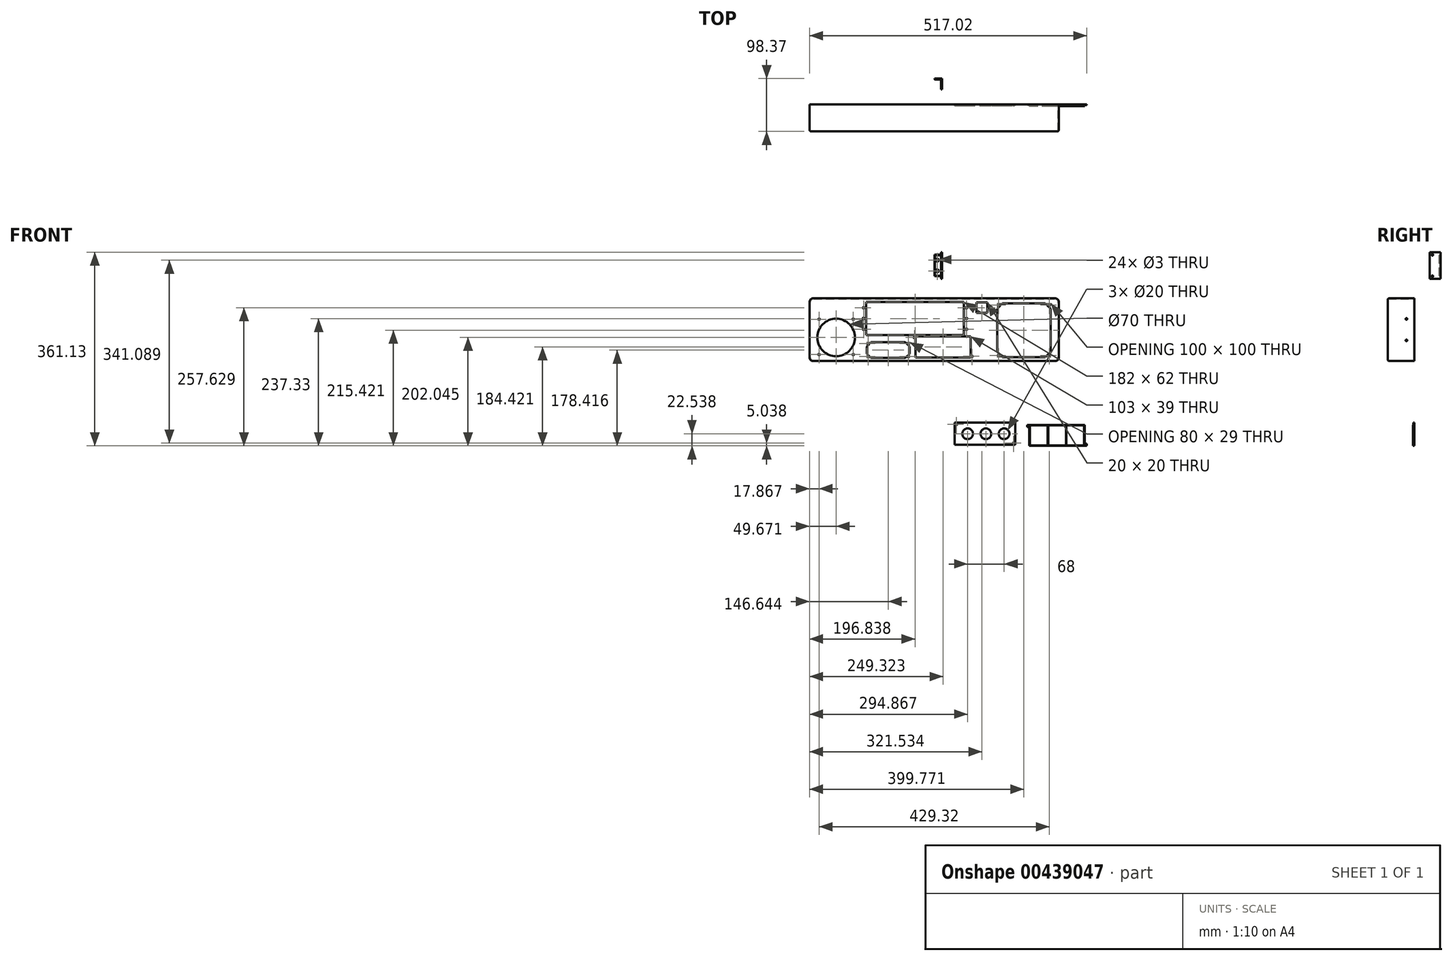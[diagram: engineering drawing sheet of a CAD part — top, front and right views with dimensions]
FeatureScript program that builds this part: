
annotation { "Feature Type Name" : "Feature", "Feature Type Description" : "" }
export const myFeature = defineFeature(function(context is Context, id is Id, definition is map)
    precondition{}
    {
        {
            var Q0;
            Q0=qCreatedBy(makeId("Front.planeOp"),FACE);
            var sketch = newSketch(context, id + "F0", { "sketchPlane" : qUnion([Q0])});
            skLineSegment(sketch, "E0.bottom", {"start": v(-245.15, 85.69) * mm, "end": v(219.85, 85.69) * mm});
            skLineSegment(sketch, "E0.top", {"start": v(-245.15, -31.31) * mm, "end": v(219.85, -31.31) * mm});
            skLineSegment(sketch, "E0.left", {"start": v(-245.15, 85.69) * mm, "end": v(-245.15, -31.31) * mm});
            skLineSegment(sketch, "E0.right", {"start": v(219.85, 85.69) * mm, "end": v(219.85, -31.31) * mm});
            skSolve(sketch);
        }
        {
            var Q0;
            Q0=qSketchRegion(id+"F0",true);
            var Q1;
            Q1=makeQuery(id+"F0.imprint","IMPRINT",FACE,{"disambiguationData":[TD([[makeQuery(id+"F0.imprint","IMPRINT",EDGE,{"derivedFrom":sQuery(id+"F0.wireOp",EDGE,"E0.bottom")}),-1.0]])]});
            extrude(context, id + "F1", {"entities" : qUnion([Q0, Q1]), "depth" : 50 * mm});
        }
        {
            var Q0;
            Q0=makeQuery(id+"F1.opExtrude","CAP_FACE",FACE,{"disambiguationData":[OSD([sQuery(id+"F0.wireOp",EDGE,"E0.bottom"),sQuery(id+"F0.wireOp",EDGE,"E0.top"),sQuery(id+"F0.wireOp",EDGE,"E0.left"),sQuery(id+"F0.wireOp",EDGE,"E0.right")])],"isStart":true});
            shell(context, id + "F2", {"entities" : qUnion([Q0]), "thickness" : 1 * mm});
        }
        {
            var Q0;
            Q0=makeQuery(id+"F1.opExtrude","CAP_FACE",FACE,{"disambiguationData":[OSD([sQuery(id+"F0.wireOp",EDGE,"E0.bottom"),sQuery(id+"F0.wireOp",EDGE,"E0.top"),sQuery(id+"F0.wireOp",EDGE,"E0.left"),sQuery(id+"F0.wireOp",EDGE,"E0.right")])],"isStart":false});
            var sketch = newSketch(context, id + "F3", { "sketchPlane" : qUnion([Q0])});
            skLineSegment(sketch, "E1.bottom", {"start": v(-139.31, 79.02) * mm, "end": v(42.69, 79.02) * mm});
            skLineSegment(sketch, "E1.top", {"start": v(-139.31, 17.02) * mm, "end": v(42.69, 17.02) * mm});
            skLineSegment(sketch, "E1.left", {"start": v(-139.31, 79.02) * mm, "end": v(-139.31, 17.02) * mm});
            skLineSegment(sketch, "E1.right", {"start": v(42.69, 79.02) * mm, "end": v(42.69, 17.02) * mm});
            skLineSegment(sketch, "E2.bottom", {"start": v(66.38, 78.32) * mm, "end": v(86.38, 78.32) * mm});
            skLineSegment(sketch, "E2.top", {"start": v(66.38, 58.32) * mm, "end": v(86.38, 58.32) * mm});
            skLineSegment(sketch, "E2.left", {"start": v(66.38, 78.32) * mm, "end": v(66.38, 58.32) * mm});
            skLineSegment(sketch, "E2.right", {"start": v(86.38, 78.32) * mm, "end": v(86.38, 58.32) * mm});
            skLineSegment(sketch, "E3.bottom", {"start": v(114.52, 76.11) * mm, "end": v(194.72, 76.11) * mm});
            skLineSegment(sketch, "E3.top", {"start": v(114.52, -23.89) * mm, "end": v(194.72, -23.89) * mm});
            skLineSegment(sketch, "E3.left", {"start": v(104.62, 66.21) * mm, "end": v(104.62, -13.99) * mm});
            skLineSegment(sketch, "E3.right", {"start": v(204.62, 66.21) * mm, "end": v(204.62, -13.99) * mm});
            skLineSegment(sketch, "E4.bottom", {"start": v(-128.05, -55.46) * mm, "end": v(-35.05, -55.46) * mm, "construction": true});
            skLineSegment(sketch, "E4.top", {"start": v(-128.05, -91.46) * mm, "end": v(-35.05, -91.46) * mm, "construction": true});
            skLineSegment(sketch, "E4.left", {"start": v(-128.05, -55.46) * mm, "end": v(-128.05, -91.46) * mm, "construction": true});
            skLineSegment(sketch, "E4.right", {"start": v(-35.05, -55.46) * mm, "end": v(-35.05, -91.46) * mm, "construction": true});
            skCircle(sketch, "E5", {"center": v(47.69, 68.02) * mm, "radius": 1.5 * mm});
            skCircle(sketch, "E6", {"center": v(47.69, 48.02) * mm, "radius": 1.5 * mm});
            skCircle(sketch, "E7", {"center": v(47.69, 28.02) * mm, "radius": 1.5 * mm});
            skLineSegment(sketch, "E8.bottom", {"start": v(-233.81, -59.67) * mm, "end": v(-156.81, -59.67) * mm, "construction": true});
            skLineSegment(sketch, "E8.top", {"start": v(-233.81, -136.67) * mm, "end": v(-156.81, -136.67) * mm, "construction": true});
            skLineSegment(sketch, "E8.left", {"start": v(-233.81, -59.67) * mm, "end": v(-233.81, -136.67) * mm, "construction": true});
            skLineSegment(sketch, "E8.right", {"start": v(-156.81, -59.67) * mm, "end": v(-156.81, -136.67) * mm, "construction": true});
            skCircle(sketch, "E9", {"center": v(107.52, 72.86) * mm, "radius": 1.5 * mm});
            skLineSegment(sketch, "E10", {"start": v(104.62, 66.21) * mm, "end": v(114.52, 76.11) * mm});
            skCircle(sketch, "E11", {"center": v(51.32, -84.07) * mm, "radius": 9.5 * mm});
            skLineSegment(sketch, "E12.bottom", {"start": v(34.38, -64.36) * mm, "end": v(127.38, -64.36) * mm});
            skLineSegment(sketch, "E12.top", {"start": v(34.38, -100.36) * mm, "end": v(127.38, -100.36) * mm});
            skLineSegment(sketch, "E12.left", {"start": v(34.38, -64.36) * mm, "end": v(34.38, -100.36) * mm});
            skLineSegment(sketch, "E12.right", {"start": v(127.38, -64.36) * mm, "end": v(127.38, -100.36) * mm});
            skCircle(sketch, "E13", {"center": v(81.35, -84.07) * mm, "radius": 9.5 * mm});
            skCircle(sketch, "E14", {"center": v(110.74, -84.07) * mm, "radius": 9.5 * mm});
            skCircle(sketch, "E15", {"center": v(38.38, -68.36) * mm, "radius": 1.5 * mm});
            skCircle(sketch, "E16", {"center": v(123.38, -96.36) * mm, "radius": 1.5 * mm});
            skLineSegment(sketch, "E17.bottom", {"start": v(-130.73, 3.6) * mm, "end": v(-66.28, 3.6) * mm});
            skLineSegment(sketch, "E17.top", {"start": v(-130.73, -25.4) * mm, "end": v(-66.28, -25.4) * mm});
            skLineSegment(sketch, "E17.left", {"start": v(-138.5, -4.17) * mm, "end": v(-138.5, -17.62) * mm});
            skLineSegment(sketch, "E17.right", {"start": v(-58.5, -4.17) * mm, "end": v(-58.5, -17.62) * mm});
            skCircle(sketch, "E18", {"center": v(-136, 1.1) * mm, "radius": 1.5 * mm});
            skCircle(sketch, "E19", {"center": v(-136, -22.9) * mm, "radius": 1.5 * mm});
            skCircle(sketch, "E20", {"center": v(-61, 1.1) * mm, "radius": 1.5 * mm});
            skCircle(sketch, "E21", {"center": v(-61, -22.9) * mm, "radius": 1.5 * mm});
            skLineSegment(sketch, "E22", {"start": v(104.62, -13.99) * mm, "end": v(114.52, -23.89) * mm});
            skLineSegment(sketch, "E23", {"start": v(194.72, -23.89) * mm, "end": v(204.62, -13.99) * mm});
            skLineSegment(sketch, "E24", {"start": v(194.72, 76.11) * mm, "end": v(204.62, 66.21) * mm});
            skCircle(sketch, "E25", {"center": v(107.52, -20.85) * mm, "radius": 1.5 * mm});
            skCircle(sketch, "E26", {"center": v(202.04, -20.85) * mm, "radius": 1.5 * mm});
            skCircle(sketch, "E27", {"center": v(202.04, 72.86) * mm, "radius": 1.5 * mm});
            skCircle(sketch, "E28", {"center": v(-195.48, 12.73) * mm, "radius": 35 * mm});
            skLineSegment(sketch, "E29", {"start": v(-138.5, -4.17) * mm, "end": v(-130.73, 3.6) * mm});
            skLineSegment(sketch, "E30", {"start": v(-66.28, 3.6) * mm, "end": v(-58.5, -4.17) * mm});
            skLineSegment(sketch, "E31", {"start": v(-58.5, -17.62) * mm, "end": v(-66.28, -25.4) * mm});
            skLineSegment(sketch, "E32", {"start": v(-138.5, -17.62) * mm, "end": v(-130.73, -25.4) * mm});
            skCircle(sketch, "E33", {"center": v(-144.31, 68.02) * mm, "radius": 1.5 * mm});
            skCircle(sketch, "E34", {"center": v(-144.31, 48.02) * mm, "radius": 1.5 * mm});
            skCircle(sketch, "E35", {"center": v(-144.31, 28.02) * mm, "radius": 1.5 * mm});
            skCircle(sketch, "E36", {"center": v(-227.28, 46.66) * mm, "radius": 1.5 * mm});
            skCircle(sketch, "E37", {"center": v(-227.28, -19.1) * mm, "radius": 1.5 * mm});
            skCircle(sketch, "E38", {"center": v(-163.64, -19.1) * mm, "radius": 1.5 * mm});
            skLineSegment(sketch, "E39.bottom", {"start": v(-52.33, 15.61) * mm, "end": v(60.67, 15.61) * mm, "construction": true});
            skLineSegment(sketch, "E39.top", {"start": v(-52.33, -25.39) * mm, "end": v(60.67, -25.39) * mm, "construction": true});
            skLineSegment(sketch, "E39.left", {"start": v(-52.33, 15.61) * mm, "end": v(-52.33, -25.39) * mm, "construction": true});
            skLineSegment(sketch, "E39.right", {"start": v(60.67, 15.61) * mm, "end": v(60.67, -25.39) * mm, "construction": true});
            skCircle(sketch, "E40", {"center": v(-163.68, 46.66) * mm, "radius": 1.5 * mm});
            skCircle(sketch, "E41", {"center": v(-49.33, 12.61) * mm, "radius": 1.5 * mm});
            skCircle(sketch, "E42", {"center": v(57.67, -22.39) * mm, "radius": 1.5 * mm});
            skLineSegment(sketch, "E43.bottom", {"start": v(-47.33, 14.61) * mm, "end": v(55.67, 14.61) * mm});
            skLineSegment(sketch, "E43.top", {"start": v(-47.33, -24.39) * mm, "end": v(55.67, -24.39) * mm});
            skLineSegment(sketch, "E43.left", {"start": v(-47.33, 14.61) * mm, "end": v(-47.33, -24.39) * mm});
            skLineSegment(sketch, "E43.right", {"start": v(55.67, 14.61) * mm, "end": v(55.67, -24.39) * mm});
            skPoint(sketch, "E44", {"position": v(-139.31, 48.02) * mm});
            skSolve(sketch);
        }
        {
            var Q0;
            Q0=makeQuery(id+"F1.opExtrude","SWEPT_EDGE",EDGE,{"disambiguationData":[OSD([sQuery(id+"F0.wireOp",EDGE,"E0.bottom"),sQuery(id+"F0.wireOp",EDGE,"E0.left")])]});
            var Q1;
            Q1=makeQuery(id+"F1.opExtrude","SWEPT_EDGE",EDGE,{"disambiguationData":[OSD([sQuery(id+"F0.wireOp",EDGE,"E0.bottom"),sQuery(id+"F0.wireOp",EDGE,"E0.right")])]});
            var Q2;
            Q2=makeQuery(id+"F1.opExtrude","SWEPT_EDGE",EDGE,{"disambiguationData":[OSD([sQuery(id+"F0.wireOp",EDGE,"E0.top"),sQuery(id+"F0.wireOp",EDGE,"E0.right")])]});
            var Q3;
            Q3=makeQuery(id+"F1.opExtrude","SWEPT_EDGE",EDGE,{"disambiguationData":[OSD([sQuery(id+"F0.wireOp",EDGE,"E0.top"),sQuery(id+"F0.wireOp",EDGE,"E0.left")])]});
            var Q4;
            Q4=makeQuery(id+"F2.opShell","OFFSET_EDGE",EDGE,{"disambiguationData":[OSD([sQuery(id+"F0.wireOp",EDGE,"E0.bottom"),sQuery(id+"F0.wireOp",EDGE,"E0.left")])]});
            var Q5;
            Q5=makeQuery(id+"F2.opShell","OFFSET_EDGE",EDGE,{"disambiguationData":[OSD([sQuery(id+"F0.wireOp",EDGE,"E0.top"),sQuery(id+"F0.wireOp",EDGE,"E0.left")])]});
            var Q6;
            Q6=makeQuery(id+"F2.opShell","OFFSET_EDGE",EDGE,{"disambiguationData":[OSD([sQuery(id+"F0.wireOp",EDGE,"E0.top"),sQuery(id+"F0.wireOp",EDGE,"E0.right")])]});
            var Q7;
            Q7=makeQuery(id+"F2.opShell","OFFSET_EDGE",EDGE,{"disambiguationData":[OSD([sQuery(id+"F0.wireOp",EDGE,"E0.bottom"),sQuery(id+"F0.wireOp",EDGE,"E0.right")])]});
            fillet(context, id + "F4", {"entities" : qUnion([Q0, Q1, Q2, Q3, Q4, Q5, Q6, Q7]), "radius" : 7 * mm, "tangentPropagation" : true, "allowEdgeOverflow" : false});
        }
        {
            var Q0;
            Q0=qSketchRegion(id+"F3",true);
            extrude(context, id + "F5", {"entities" : qUnion([Q0]), "operationType" : NewBodyOperationType.REMOVE, "oppositeDirection" : true, "depth" : 25 * mm});
        }
        {
            var Q0;
            {var subQ0=sQuery(id+"F0.wireOp",EDGE,"E0.right");var subQ1=sQuery(id+"F0.wireOp",EDGE,"E0.bottom");Q0=makeQuery(id+"F4.opFillet","BLEND_EDGE",EDGE,{"blendedFrom":[makeQuery(id+"F1.opExtrude","SWEPT_EDGE",EDGE,{"disambiguationData":[OSD([subQ1,subQ0])]}),makeQuery(id+"F1.opExtrude","CAP_FACE",FACE,{"disambiguationData":[OSD([subQ1,sQuery(id+"F0.wireOp",EDGE,"E0.top"),sQuery(id+"F0.wireOp",EDGE,"E0.left"),subQ0])],"isStart":false})],"blendedInto":[makeQuery(id+"F1.opExtrude","CAP_FACE",FACE,{"disambiguationData":[OSD([subQ1,sQuery(id+"F0.wireOp",EDGE,"E0.top"),sQuery(id+"F0.wireOp",EDGE,"E0.left"),subQ0])],"isStart":false})]});}
            fillet(context, id + "F6", {"entities" : qUnion([Q0]), "radius" : 3 * mm, "tangentPropagation" : true, "allowEdgeOverflow" : false});
        }
        {
            var Q0;
            Q0=makeQuery(id+"F1.opExtrude","CAP_FACE",FACE,{"disambiguationData":[OSD([sQuery(id+"F0.wireOp",EDGE,"E0.bottom"),sQuery(id+"F0.wireOp",EDGE,"E0.top"),sQuery(id+"F0.wireOp",EDGE,"E0.left"),sQuery(id+"F0.wireOp",EDGE,"E0.right")])],"isStart":false});
            var sketch = newSketch(context, id + "F7", { "sketchPlane" : qUnion([Q0])});
            skLineSegment(sketch, "E45.bottom", {"start": v(216.55, -24.6) * mm, "end": v(89.55, -24.6) * mm});
            skLineSegment(sketch, "E45.top", {"start": v(216.55, 75.4) * mm, "end": v(89.55, 75.4) * mm});
            skLineSegment(sketch, "E45.left", {"start": v(216.55, -24.6) * mm, "end": v(216.55, 75.4) * mm});
            skLineSegment(sketch, "E45.right", {"start": v(89.55, -24.6) * mm, "end": v(89.55, 75.4) * mm});
            skLineSegment(sketch, "E46.bottom", {"start": v(-397.12, -53.44) * mm, "end": v(-332.84, -53.44) * mm});
            skLineSegment(sketch, "E46.top", {"start": v(-397.12, -159.24) * mm, "end": v(-332.84, -159.24) * mm});
            skLineSegment(sketch, "E46.left", {"start": v(-397.12, -53.44) * mm, "end": v(-397.12, -159.24) * mm});
            skLineSegment(sketch, "E46.right", {"start": v(-332.84, -53.44) * mm, "end": v(-332.84, -159.24) * mm});
            skLineSegment(sketch, "E47.bottom", {"start": v(38.72, -106.98) * mm, "end": v(60.72, -106.98) * mm, "construction": true});
            skLineSegment(sketch, "E47.top", {"start": v(38.72, -136.98) * mm, "end": v(60.72, -136.98) * mm, "construction": true});
            skLineSegment(sketch, "E47.left", {"start": v(38.72, -106.98) * mm, "end": v(38.72, -136.98) * mm, "construction": true});
            skLineSegment(sketch, "E47.right", {"start": v(60.72, -106.98) * mm, "end": v(60.72, -136.98) * mm, "construction": true});
            skLineSegment(sketch, "E48.bottom", {"start": v(-233.32, 82.69) * mm, "end": v(-155.32, 82.69) * mm});
            skLineSegment(sketch, "E48.top", {"start": v(-233.32, -28.31) * mm, "end": v(-155.32, -28.31) * mm});
            skLineSegment(sketch, "E48.left", {"start": v(-233.32, 82.69) * mm, "end": v(-233.32, -28.31) * mm});
            skLineSegment(sketch, "E48.right", {"start": v(-155.32, 82.69) * mm, "end": v(-155.32, -28.31) * mm});
            skLineSegment(sketch, "E49.bottom", {"start": v(31.72, -103.48) * mm, "end": v(64.72, -103.48) * mm, "construction": true});
            skLineSegment(sketch, "E49.top", {"start": v(31.72, -140.48) * mm, "end": v(64.72, -140.48) * mm, "construction": true});
            skLineSegment(sketch, "E49.left", {"start": v(31.72, -103.48) * mm, "end": v(31.72, -140.48) * mm, "construction": true});
            skLineSegment(sketch, "E49.right", {"start": v(64.72, -103.48) * mm, "end": v(64.72, -140.48) * mm, "construction": true});
            skLineSegment(sketch, "E50.bottom", {"start": v(72.72, -106.98) * mm, "end": v(94.72, -106.98) * mm, "construction": true});
            skLineSegment(sketch, "E50.top", {"start": v(72.72, -136.98) * mm, "end": v(94.72, -136.98) * mm, "construction": true});
            skLineSegment(sketch, "E50.left", {"start": v(72.72, -106.98) * mm, "end": v(72.72, -136.98) * mm, "construction": true});
            skLineSegment(sketch, "E50.right", {"start": v(94.72, -106.98) * mm, "end": v(94.72, -136.98) * mm, "construction": true});
            skLineSegment(sketch, "E51.bottom", {"start": v(65.72, -103.48) * mm, "end": v(98.72, -103.48) * mm, "construction": true});
            skLineSegment(sketch, "E51.top", {"start": v(65.72, -140.48) * mm, "end": v(98.72, -140.48) * mm, "construction": true});
            skLineSegment(sketch, "E51.left", {"start": v(65.72, -103.48) * mm, "end": v(65.72, -140.48) * mm, "construction": true});
            skLineSegment(sketch, "E51.right", {"start": v(98.72, -103.48) * mm, "end": v(98.72, -140.48) * mm, "construction": true});
            skLineSegment(sketch, "E52.bottom", {"start": v(106.72, -106.98) * mm, "end": v(128.72, -106.98) * mm, "construction": true});
            skLineSegment(sketch, "E52.top", {"start": v(106.72, -136.98) * mm, "end": v(128.72, -136.98) * mm, "construction": true});
            skLineSegment(sketch, "E52.left", {"start": v(106.72, -106.98) * mm, "end": v(106.72, -136.98) * mm, "construction": true});
            skLineSegment(sketch, "E52.right", {"start": v(128.72, -106.98) * mm, "end": v(128.72, -136.98) * mm, "construction": true});
            skLineSegment(sketch, "E53.bottom", {"start": v(99.72, -103.48) * mm, "end": v(132.72, -103.48) * mm, "construction": true});
            skLineSegment(sketch, "E53.top", {"start": v(99.72, -140.48) * mm, "end": v(132.72, -140.48) * mm, "construction": true});
            skLineSegment(sketch, "E53.left", {"start": v(99.72, -103.48) * mm, "end": v(99.72, -140.48) * mm, "construction": true});
            skLineSegment(sketch, "E53.right", {"start": v(132.72, -103.48) * mm, "end": v(132.72, -140.48) * mm, "construction": true});
            skCircle(sketch, "E54", {"center": v(83.72, -121.98) * mm, "radius": 10 * mm});
            skCircle(sketch, "E55", {"center": v(49.72, -121.98) * mm, "radius": 10 * mm});
            skCircle(sketch, "E56", {"center": v(117.72, -121.98) * mm, "radius": 10 * mm});
            skLineSegment(sketch, "E57.bottom", {"start": v(-253.05, -28.31) * mm, "end": v(-331.05, -28.31) * mm});
            skLineSegment(sketch, "E57.top", {"start": v(-253.05, 91.69) * mm, "end": v(-331.05, 91.69) * mm});
            skLineSegment(sketch, "E57.left", {"start": v(-253.05, -28.31) * mm, "end": v(-253.05, 91.69) * mm});
            skLineSegment(sketch, "E57.right", {"start": v(-331.05, -28.31) * mm, "end": v(-331.05, 91.69) * mm});
            skSolve(sketch);
        }
        {
            var Q0;
            Q0=makeQuery(id+"F1.opExtrude","SWEPT_FACE",FACE,{"disambiguationData":[OSD([sQuery(id+"F0.wireOp",EDGE,"E0.left")])]});
            var sketch = newSketch(context, id + "F8", { "sketchPlane" : qUnion([Q0])});
            skCircle(sketch, "E58", {"center": v(15, 47.19) * mm, "radius": 1.5 * mm});
            skCircle(sketch, "E59", {"center": v(15, 7.19) * mm, "radius": 1.5 * mm});
            skLineSegment(sketch, "E60", {"start": v(-16.01, 27.19) * mm, "end": v(37.35, 27.19) * mm, "construction": true});
            skPoint(sketch, "E61.middle.positionSnap0", {"position": v(0, 27.19) * mm});
            skPoint(sketch, "E61.centerSnap0", {"position": v(0, 27.19) * mm});
            skLineSegment(sketch, "E62.bottom", {"start": v(3, 6.19) * mm, "end": v(0, 6.19) * mm, "construction": true});
            skLineSegment(sketch, "E62.top", {"start": v(3, 48.19) * mm, "end": v(0, 48.19) * mm, "construction": true});
            skLineSegment(sketch, "E62.left", {"start": v(3, 6.19) * mm, "end": v(3, 48.19) * mm, "construction": true});
            skLineSegment(sketch, "E62.right", {"start": v(0, 6.19) * mm, "end": v(0, 48.19) * mm, "construction": true});
            skPoint(sketch, "E62.middle", {"position": v(1.5, 27.19) * mm});
            skSolve(sketch);
        }
        {
            var Q0;
            Q0=qSketchRegion(id+"F8",true);
            extrude(context, id + "F9", {"entities" : qUnion([Q0]), "operationType" : NewBodyOperationType.REMOVE, "oppositeDirection" : true, "depth" : 500 * mm});
        }
        {
            var Q0;
            Q0=qCreatedBy(makeId("Right.planeOp"),FACE);
            var sketch = newSketch(context, id + "F10", { "sketchPlane" : qUnion([Q0])});
            skLineSegment(sketch, "E63.bottom", {"start": v(28.37, 121.82) * mm, "end": v(48.37, 121.82) * mm});
            skLineSegment(sketch, "E63.top", {"start": v(28.37, 171.82) * mm, "end": v(48.37, 171.82) * mm});
            skLineSegment(sketch, "E63.left", {"start": v(28.37, 121.82) * mm, "end": v(28.37, 171.82) * mm});
            skLineSegment(sketch, "E63.right", {"start": v(48.37, 121.82) * mm, "end": v(48.37, 171.82) * mm});
            skPoint(sketch, "E63.middle", {"position": v(38.37, 146.82) * mm});
            skCircle(sketch, "E64", {"center": v(33.37, 166.82) * mm, "radius": 1.5 * mm});
            skCircle(sketch, "E65", {"center": v(33.37, 126.82) * mm, "radius": 1.5 * mm});
            skSolve(sketch);
        }
        {
            var Q0;
            Q0=qSketchRegion(id+"F10",true);
            extrude(context, id + "F11", {"entities" : qUnion([Q0]), "depth" : 2 * mm});
        }
        {
            var Q0;
            Q0=makeQuery(id+"F11.opExtrude","SWEPT_FACE",FACE,{"disambiguationData":[OSD([sQuery(id+"F10.wireOp",EDGE,"E63.right")])]});
            var sketch = newSketch(context, id + "F12", { "sketchPlane" : qUnion([Q0])});
            skLineSegment(sketch, "E66.bottom", {"start": v(0, 166.82) * mm, "end": v(12, 166.82) * mm});
            skLineSegment(sketch, "E66.top", {"start": v(0, 126.82) * mm, "end": v(12, 126.82) * mm});
            skLineSegment(sketch, "E66.left", {"start": v(0, 166.82) * mm, "end": v(0, 126.82) * mm});
            skLineSegment(sketch, "E66.right", {"start": v(12, 166.82) * mm, "end": v(12, 126.82) * mm});
            skSolve(sketch);
        }
        {
            var Q0;
            Q0=qSketchRegion(id+"F12",true);
            extrude(context, id + "F13", {"entities" : qUnion([Q0]), "operationType" : NewBodyOperationType.ADD, "oppositeDirection" : true, "depth" : 2 * mm});
        }
        {
            var Q0;
            Q0=makeQuery(id+"F13.opExtrude","CAP_FACE",FACE,{"disambiguationData":[OSD([sQuery(id+"F12.wireOp",EDGE,"E66.bottom"),sQuery(id+"F12.wireOp",EDGE,"E66.top"),sQuery(id+"F12.wireOp",EDGE,"E66.left"),sQuery(id+"F12.wireOp",EDGE,"E66.right")])],"isStart":false});
            var sketch = newSketch(context, id + "F14", { "sketchPlane" : qUnion([Q0])});
            skCircle(sketch, "E67", {"center": v(-7, 156.82) * mm, "radius": 1.5 * mm});
            skCircle(sketch, "E68", {"center": v(-7, 136.82) * mm, "radius": 1.5 * mm});
            skSolve(sketch);
        }
        {
            var Q0;
            Q0=sQuery(id+"F14.wireOp",VERTEX,"E67.center");
            var Q1;
            Q1=sQuery(id+"F14.wireOp",VERTEX,"E68.center");
            var Q2;
            Q2=makeQuery(id+"F11.opExtrude","SWEPT_BODY",BODY,{"disambiguationData":[OSD([sQuery(id+"F10.wireOp",EDGE,"E63.bottom"),sQuery(id+"F10.wireOp",EDGE,"E63.top"),sQuery(id+"F10.wireOp",EDGE,"E63.left"),sQuery(id+"F10.wireOp",EDGE,"E63.right"),sQuery(id+"F10.wireOp",EDGE,"E64"),sQuery(id+"F10.wireOp",EDGE,"E65")])]});
            hole(context, id + "F15", {"style" : HoleStyle.C_SINK, "endStyle" : HoleEndStyle.THROUGH, "holeDiameter" : 3 * mm, "cSinkDiameter" : 5.7 * mm, "cSinkAngle" : 90 * degree, "locations" : qUnion([Q0, Q1]), "scope" : qUnion([Q2]), "isTappedThrough" : true});
        }
        {
            var Q0;
            Q0=makeQuery(id+"F13.opExtrude","CAP_EDGE",EDGE,{"disambiguationData":[OSD([sQuery(id+"F12.wireOp",EDGE,"E66.bottom")])],"isStart":false});
            var Q1;
            Q1=makeQuery(id+"F13.opExtrude","CAP_EDGE",EDGE,{"disambiguationData":[OSD([sQuery(id+"F12.wireOp",EDGE,"E66.right")])],"isStart":false});
            var Q2;
            Q2=makeQuery(id+"F13.opExtrude","CAP_EDGE",EDGE,{"disambiguationData":[OSD([sQuery(id+"F12.wireOp",EDGE,"E66.top")])],"isStart":false});
            chamfer(context, id + "F16", {"entities" : qUnion([Q0, Q1, Q2]), "width" : 1 * mm, "tangentPropagation" : true});
        }
        {
            var Q0;
            Q0=qCreatedBy(makeId("Front.planeOp"),FACE);
            var sketch = newSketch(context, id + "F17", { "sketchPlane" : qUnion([Q0])});
            skCircle(sketch, "E69", {"center": v(49.72, -166.77) * mm, "radius": 10 * mm});
            skCircle(sketch, "E70", {"center": v(83.72, -166.77) * mm, "radius": 10 * mm});
            skCircle(sketch, "E71", {"center": v(117.72, -166.77) * mm, "radius": 10 * mm});
            skCircle(sketch, "E72", {"center": v(28.72, -149.27) * mm, "radius": 1.5 * mm});
            skCircle(sketch, "E73", {"center": v(135.72, -184.27) * mm, "radius": 1.5 * mm});
            skLineSegment(sketch, "E74.bottom", {"start": v(25.72, -146.27) * mm, "end": v(138.72, -146.27) * mm});
            skLineSegment(sketch, "E74.top", {"start": v(25.72, -187.27) * mm, "end": v(138.72, -187.27) * mm});
            skLineSegment(sketch, "E74.left", {"start": v(25.72, -146.27) * mm, "end": v(25.72, -187.27) * mm});
            skLineSegment(sketch, "E74.right", {"start": v(138.72, -146.27) * mm, "end": v(138.72, -187.27) * mm});
            skSolve(sketch);
        }
        {
            var Q0;
            Q0=makeQuery(id+"F17.imprint","IMPRINT",FACE,{"disambiguationData":[TD([[makeQuery(id+"F17.imprint","IMPRINT",EDGE,{"derivedFrom":sQuery(id+"F17.wireOp",EDGE,"E69")}),-1.0]])]});
            extrude(context, id + "F18", {"entities" : qUnion([Q0]), "depth" : 2 * mm});
        }
        {
            var Q0;
            Q0=qCreatedBy(makeId("Front.planeOp"),FACE);
            var sketch = newSketch(context, id + "F19", { "sketchPlane" : qUnion([Q0])});
            skLineSegment(sketch, "E75.bottom", {"start": v(164.87, -150.31) * mm, "end": v(267.87, -150.31) * mm});
            skLineSegment(sketch, "E75.top", {"start": v(164.87, -189.31) * mm, "end": v(267.87, -189.31) * mm});
            skLineSegment(sketch, "E75.left", {"start": v(164.87, -150.31) * mm, "end": v(164.87, -189.31) * mm});
            skLineSegment(sketch, "E75.right", {"start": v(267.87, -150.31) * mm, "end": v(267.87, -189.31) * mm});
            skLineSegment(sketch, "E76.bottom", {"start": v(164.87, -150.31) * mm, "end": v(160.87, -150.31) * mm});
            skLineSegment(sketch, "E76.top", {"start": v(164.87, -154.31) * mm, "end": v(160.87, -154.31) * mm});
            skLineSegment(sketch, "E76.left", {"start": v(164.87, -150.31) * mm, "end": v(164.87, -154.31) * mm});
            skLineSegment(sketch, "E76.right", {"start": v(160.87, -150.31) * mm, "end": v(160.87, -154.31) * mm});
            skLineSegment(sketch, "E77.bottom", {"start": v(267.87, -189.31) * mm, "end": v(271.87, -189.31) * mm});
            skLineSegment(sketch, "E77.top", {"start": v(267.87, -185.31) * mm, "end": v(271.87, -185.31) * mm});
            skLineSegment(sketch, "E77.left", {"start": v(267.87, -189.31) * mm, "end": v(267.87, -185.31) * mm});
            skLineSegment(sketch, "E77.right", {"start": v(271.87, -189.31) * mm, "end": v(271.87, -185.31) * mm});
            skCircle(sketch, "E78", {"center": v(162.87, -152.31) * mm, "radius": 1.5 * mm});
            skCircle(sketch, "E79", {"center": v(269.87, -187.31) * mm, "radius": 1.5 * mm});
            skSolve(sketch);
        }
        {
            var Q0;
            Q0=makeQuery(id+"F19.imprint","IMPRINT",FACE,{"disambiguationData":[TD([[makeQuery(id+"F19.imprint","IMPRINT",EDGE,{"derivedFrom":sQuery(id+"F19.wireOp",EDGE,"E75.bottom")}),-1.0]])]});
            extrude(context, id + "F20", {"entities" : qUnion([Q0]), "depth" : 3 * mm});
        }
        {
            var Q0;
            Q0=makeQuery(id+"F19.imprint","IMPRINT",FACE,{"disambiguationData":[TD([[makeQuery(id+"F19.imprint","IMPRINT",EDGE,{"derivedFrom":sQuery(id+"F19.wireOp",EDGE,"E76.bottom")}),1.0]])]});
            var Q1;
            Q1=makeQuery(id+"F19.imprint","IMPRINT",FACE,{"disambiguationData":[TD([[makeQuery(id+"F19.imprint","IMPRINT",EDGE,{"derivedFrom":sQuery(id+"F19.wireOp",EDGE,"E77.bottom")}),1.0]])]});
            extrude(context, id + "F21", {"entities" : qUnion([Q0, Q1]), "operationType" : NewBodyOperationType.ADD, "depth" : 1 * mm});
        }
        {
            var Q0;
            Q0=makeQuery(id+"F20.opExtrude","CAP_FACE",FACE,{"disambiguationData":[OSD([sQuery(id+"F19.wireOp",EDGE,"E75.bottom"),sQuery(id+"F19.wireOp",EDGE,"E75.top"),sQuery(id+"F19.wireOp",EDGE,"E75.left"),sQuery(id+"F19.wireOp",EDGE,"E75.right"),sQuery(id+"F19.wireOp",EDGE,"E76.left"),sQuery(id+"F19.wireOp",EDGE,"E77.left")])],"isStart":false});
            var sketch = newSketch(context, id + "F22", { "sketchPlane" : qUnion([Q0])});
            skLineSegment(sketch, "E80.bottom", {"start": v(165.87, -151.31) * mm, "end": v(198.87, -151.31) * mm});
            skLineSegment(sketch, "E80.top", {"start": v(165.87, -188.31) * mm, "end": v(198.87, -188.31) * mm});
            skLineSegment(sketch, "E80.left", {"start": v(165.87, -151.31) * mm, "end": v(165.87, -188.31) * mm});
            skLineSegment(sketch, "E80.right", {"start": v(198.87, -151.31) * mm, "end": v(198.87, -188.31) * mm});
            skLineSegment(sketch, "E81.bottom", {"start": v(199.87, -151.31) * mm, "end": v(232.87, -151.31) * mm});
            skLineSegment(sketch, "E81.top", {"start": v(199.87, -188.31) * mm, "end": v(232.87, -188.31) * mm});
            skLineSegment(sketch, "E81.left", {"start": v(199.87, -151.31) * mm, "end": v(199.87, -188.31) * mm});
            skLineSegment(sketch, "E81.right", {"start": v(232.87, -151.31) * mm, "end": v(232.87, -188.31) * mm});
            skLineSegment(sketch, "E82.bottom", {"start": v(233.87, -151.31) * mm, "end": v(266.87, -151.31) * mm});
            skLineSegment(sketch, "E82.top", {"start": v(233.87, -188.31) * mm, "end": v(266.87, -188.31) * mm});
            skLineSegment(sketch, "E82.left", {"start": v(233.87, -151.31) * mm, "end": v(233.87, -188.31) * mm});
            skLineSegment(sketch, "E82.right", {"start": v(266.87, -151.31) * mm, "end": v(266.87, -188.31) * mm});
            skLineSegment(sketch, "E83.bottom", {"start": v(198.87, -161.31) * mm, "end": v(199.87, -161.31) * mm});
            skLineSegment(sketch, "E83.top", {"start": v(198.87, -178.31) * mm, "end": v(199.87, -178.31) * mm});
            skLineSegment(sketch, "E83.left", {"start": v(198.87, -161.31) * mm, "end": v(198.87, -178.31) * mm});
            skLineSegment(sketch, "E83.right", {"start": v(199.87, -161.31) * mm, "end": v(199.87, -178.31) * mm});
            skLineSegment(sketch, "E84.bottom", {"start": v(232.87, -161.31) * mm, "end": v(233.87, -161.31) * mm});
            skLineSegment(sketch, "E84.top", {"start": v(232.87, -178.31) * mm, "end": v(233.87, -178.31) * mm});
            skLineSegment(sketch, "E84.left", {"start": v(232.87, -161.31) * mm, "end": v(232.87, -178.31) * mm});
            skLineSegment(sketch, "E84.right", {"start": v(233.87, -161.31) * mm, "end": v(233.87, -178.31) * mm});
            skSolve(sketch);
        }
        {
            var Q0;
            {var subQ1=sQuery(id+"F22.wireOp",EDGE,"E80.bottom");Q0=makeQuery(id+"F22.imprint","IMPRINT",FACE,{"disambiguationData":[TD([[makeQuery(id+"F22.imprint","IMPRINT",EDGE,{"derivedFrom":subQ1}),-1.0]])]});}
            var Q1;
            {var subQ3=sQuery(id+"F22.wireOp",EDGE,"E81.bottom");Q1=makeQuery(id+"F22.imprint","IMPRINT",FACE,{"disambiguationData":[TD([[makeQuery(id+"F22.imprint","IMPRINT",EDGE,{"derivedFrom":subQ3}),-1.0]])]});}
            var Q2;
            {var subQ1=sQuery(id+"F22.wireOp",EDGE,"E82.bottom");Q2=makeQuery(id+"F22.imprint","IMPRINT",FACE,{"disambiguationData":[TD([[makeQuery(id+"F22.imprint","IMPRINT",EDGE,{"derivedFrom":subQ1}),-1.0]])]});}
            extrude(context, id + "F23", {"entities" : qUnion([Q0, Q1, Q2]), "operationType" : NewBodyOperationType.REMOVE, "oppositeDirection" : true, "depth" : 2 * mm});
        }
        {
            var Q0;
            Q0=makeQuery(id+"F22.imprint","IMPRINT",FACE,{"disambiguationData":[TD([[makeQuery(id+"F22.imprint","IMPRINT",EDGE,{"derivedFrom":sQuery(id+"F22.wireOp",EDGE,"E83.bottom")}),-1.0]])]});
            var Q1;
            Q1=makeQuery(id+"F22.imprint","IMPRINT",FACE,{"disambiguationData":[TD([[makeQuery(id+"F22.imprint","IMPRINT",EDGE,{"derivedFrom":sQuery(id+"F22.wireOp",EDGE,"E84.bottom")}),-1.0]])]});
            extrude(context, id + "F24", {"entities" : qUnion([Q0, Q1]), "operationType" : NewBodyOperationType.REMOVE, "oppositeDirection" : true, "depth" : 3 * mm});
        }
    });
